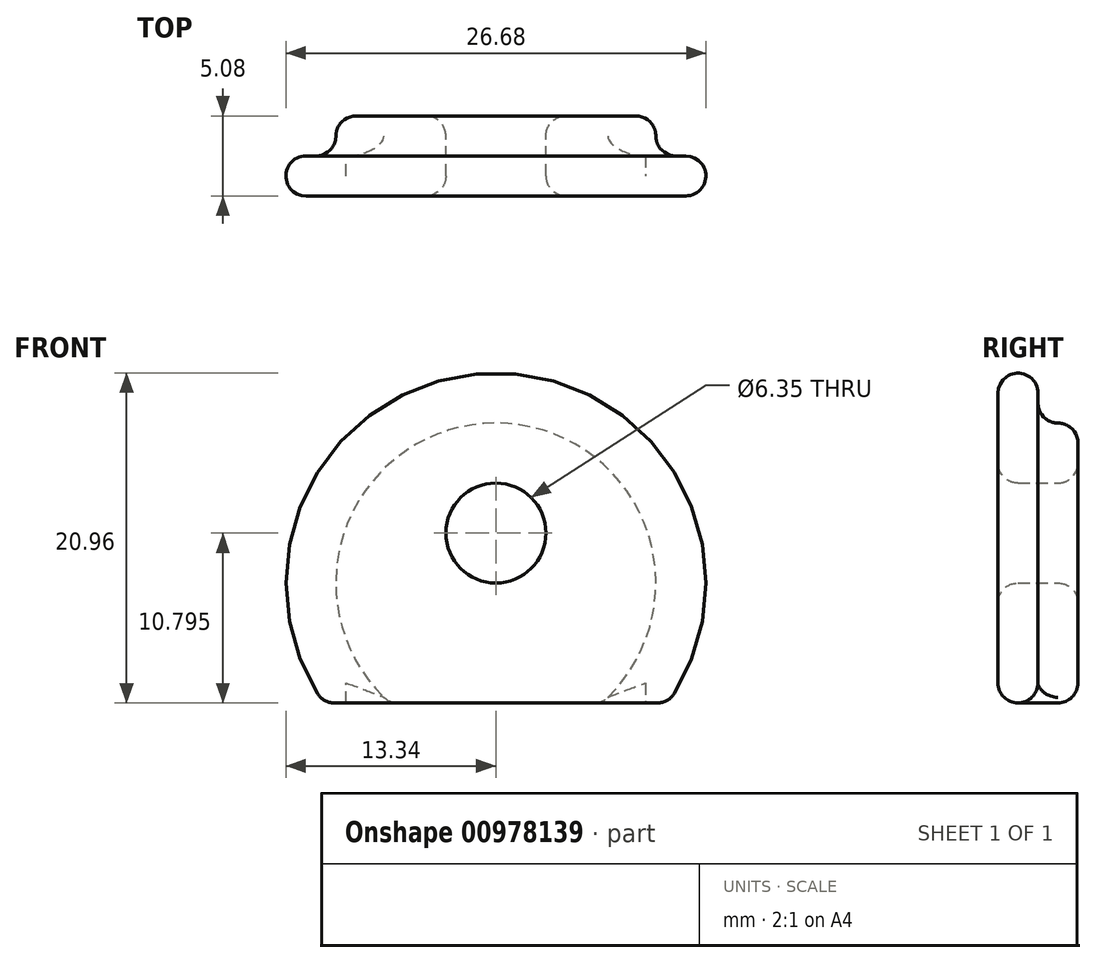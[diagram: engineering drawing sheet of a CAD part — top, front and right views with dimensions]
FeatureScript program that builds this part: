
annotation { "Feature Type Name" : "Feature", "Feature Type Description" : "" }
export const myFeature = defineFeature(function(context is Context, id is Id, definition is map)
    precondition{}
    {
        {
            var Q0;
            Q0=qCreatedBy(makeId("Front.planeOp"),FACE);
            var sketch = newSketch(context, id + "F0", { "sketchPlane" : qUnion([Q0])});
            skArc(sketch, "E0", {"start": v(6.72, -7.62) * mm, "mid": v(0, 10.16) * mm, "end": v(-6.72, -7.62) * mm});
            skLineSegment(sketch, "E1", {"start": v(-6.72, -7.62) * mm, "end": v(6.72, -7.62) * mm});
            skLineSegment(sketch, "E2", {"start": v(0, 10.16) * mm, "end": v(0, -7.62) * mm, "construction": true});
            skSolve(sketch);
        }
        {
            var Q0;
            Q0 = qSketchRegion(id + "F0", true);
            extrude(context, id + "F1", {"entities" : qUnion([Q0]), "depth" : 2.54 * mm, "offsetDistance" : 25.4 * mm});
        }
        {
            var Q0;
            Q0=makeQuery(id+"F1.opExtrude","CAP_FACE",FACE,{"disambiguationData":[OSD([sQuery(id+"F0.wireOp",EDGE,"E0"),sQuery(id+"F0.wireOp",EDGE,"E1")])],"isStart":false});
            var sketch = newSketch(context, id + "F2", { "sketchPlane" : qUnion([Q0])});
            skArc(sketch, "E3.0", {"start": v(10.94, -7.62) * mm, "mid": v(0, 13.34) * mm, "end": v(-10.94, -7.62) * mm});
            skLineSegment(sketch, "E4", {"start": v(-10.94, -7.62) * mm, "end": v(10.94, -7.62) * mm});
            skSolve(sketch);
        }
        {
            var Q0;
            {var subQ1=makeQuery(id+"F1.opExtrude","CAP_EDGE",EDGE,{"disambiguationData":[OSD([sQuery(id+"F0.wireOp",EDGE,"E0")])],"isStart":false});Q0=makeQuery(id+"F2.imprint","IMPRINT",FACE,{"disambiguationData":[TD([[makeQuery(id+"F2.imprint","IMPRINT",EDGE,{"derivedFrom":subQ1}),1.0]])]});}
            var Q1;
            {var subQ0=sQuery(id+"F2.wireOp",EDGE,"E3.0");Q1=makeQuery(id+"F2.imprint","IMPRINT",FACE,{"disambiguationData":[TD([[makeQuery(id+"F2.imprint","IMPRINT",EDGE,{"derivedFrom":subQ0}),1.0]])]});}
            var Q2;
            Q2=sQuery(id+"F2.wireOp",EDGE,"E4");
            extrude(context, id + "F3", {"entities" : qUnion([Q0, Q1]), "operationType" : NewBodyOperationType.ADD, "surfaceEntities" : qUnion([Q2]), "depth" : 2.54 * mm, "offsetDistance" : 25.4 * mm});
        }
        {
            var Q0;
            Q0=makeQuery(id+"F1.opExtrude","CAP_FACE",FACE,{"disambiguationData":[OSD([sQuery(id+"F0.wireOp",EDGE,"E0"),sQuery(id+"F0.wireOp",EDGE,"E1")])],"isStart":true});
            var sketch = newSketch(context, id + "F4", { "sketchPlane" : qUnion([Q0])});
            skCircle(sketch, "E5", {"center": v(0, 3.18) * mm, "radius": 3.18 * mm});
            skSolve(sketch);
        }
        {
            var Q0;
            Q0 = qSketchRegion(id + "F4", true);
            extrude(context, id + "F5", {"entities" : qUnion([Q0]), "operationType" : NewBodyOperationType.REMOVE, "endBound" : BoundingType.THROUGH_ALL, "oppositeDirection" : true, "depth" : 25.4 * mm, "offsetDistance" : 25.4 * mm});
        }
        {
            var Q0;
            Q0=makeQuery(id+"F1.opExtrude","CAP_FACE",FACE,{"disambiguationData":[OSD([sQuery(id+"F0.wireOp",EDGE,"E0"),sQuery(id+"F0.wireOp",EDGE,"E1")])],"isStart":true});
            var Q1;
            Q1=makeQuery(id+"F3.opExtrude","CAP_FACE",FACE,{"disambiguationData":[OSD([sQuery(id+"F2.wireOp",EDGE,"E3.0"),sQuery(id+"F2.wireOp",EDGE,"E4")])],"isStart":false});
            var Q2;
            Q2=makeQuery(id+"F3.opExtrude","CAP_FACE",FACE,{"disambiguationData":[OSD([sQuery(id+"F2.wireOp",EDGE,"E3.0"),sQuery(id+"F2.wireOp",EDGE,"E4")])],"isStart":true});
            var Q3;
            Q3=makeQuery(id+"F3.boolean.opBoolean","MERGE",FACE,{"derivedFrom":[makeQuery(id+"F1.opExtrude","SWEPT_FACE",FACE,{"disambiguationData":[OSD([sQuery(id+"F0.wireOp",EDGE,"E1")])]}),makeQuery(id+"F3.opExtrude","SWEPT_FACE",FACE,{"disambiguationData":[OSD([sQuery(id+"F2.wireOp",EDGE,"E4")])]})]});
            fillet(context, id + "F6", {"entities" : qUnion([Q0, Q1, Q2, Q3]), "radius" : 1.27 * mm, "tangentPropagation" : true, "allowEdgeOverflow" : false});
        }
    });
